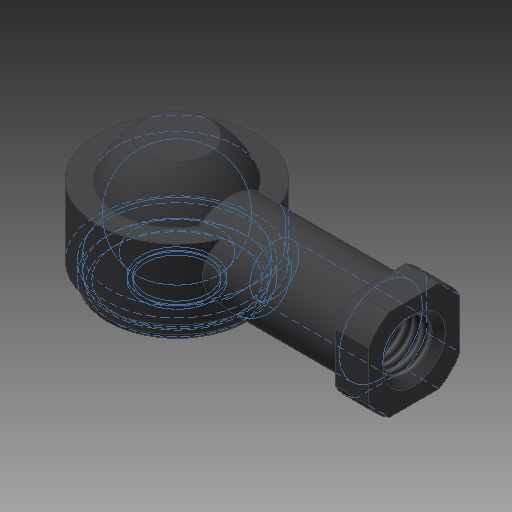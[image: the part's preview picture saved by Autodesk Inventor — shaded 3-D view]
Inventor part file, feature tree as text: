
AUTODESK INVENTOR PART (.ipt)
format: ipt  version: 2018 (Build 220112000, 112)  size: 253,952 bytes
history: native  units: mm
features: sketch x9, other x7, revolve x6, extrude x2, hole x1
ambient origin geometry x8: Origin, YZ Plane, XZ Plane, XY Plane, X Axis, Y Axis, Z Axis, Center Point
bodies: Solid1 (feature_tree)
feature tree (25):
  revolve  "Revolution1"  [1 undecoded]
  extrude  "Extrusion1"  TaperAngle=360.0deg  [1 undecoded]
  revolve  "Revolution2"  Angle=360.0deg
  revolve  "Revolution3"  [1 undecoded]
  revolve  "Revolution4"  [1 undecoded]
  revolve  "Revolution5"  [1 undecoded]
  revolve  "Revolution6"  [1 undecoded]
  hole  "Hole1"  [1 undecoded]
  extrude  "Extrusion2"  [1 undecoded]
  other  "IP1_XY"
  other  "IP1_YZ"
  other  "IP1_ZX"
  other  "IP1_X"
  other  "IP1_Y"
  other  "IP1_Z"
  other  "IP1_Center"
  sketch  "Sketch_2"  dims[d0=360.0deg d1=50.0mm d2=0.0mm]
  sketch  "Sketch_16"
  sketch  "Sketch_12"  dims[d5=360.0deg d6=360.0deg]
  sketch  "Sketch_13"  dims[d7=360.0deg]
  sketch  "Sketch_14"  dims[d8=11.835mm d9=31.0825mm d10=15.0mm d11=2.0mm d12=90.0deg d13=33.5825mm d14=120.0deg d15=8.0mm d16=0.0mm]
  sketch  "Sketch_15"
  sketch  "Sketch_17"
  sketch  "Sketch8"  dims[d3=360.0deg d4=360.0deg]
  sketch  "Sketch_20"
note: 8 required parameter values undecoded (feature->parameter linkage not recoverable at this tier; creation-order binding heuristic only, values carry confidence <= 0.55)